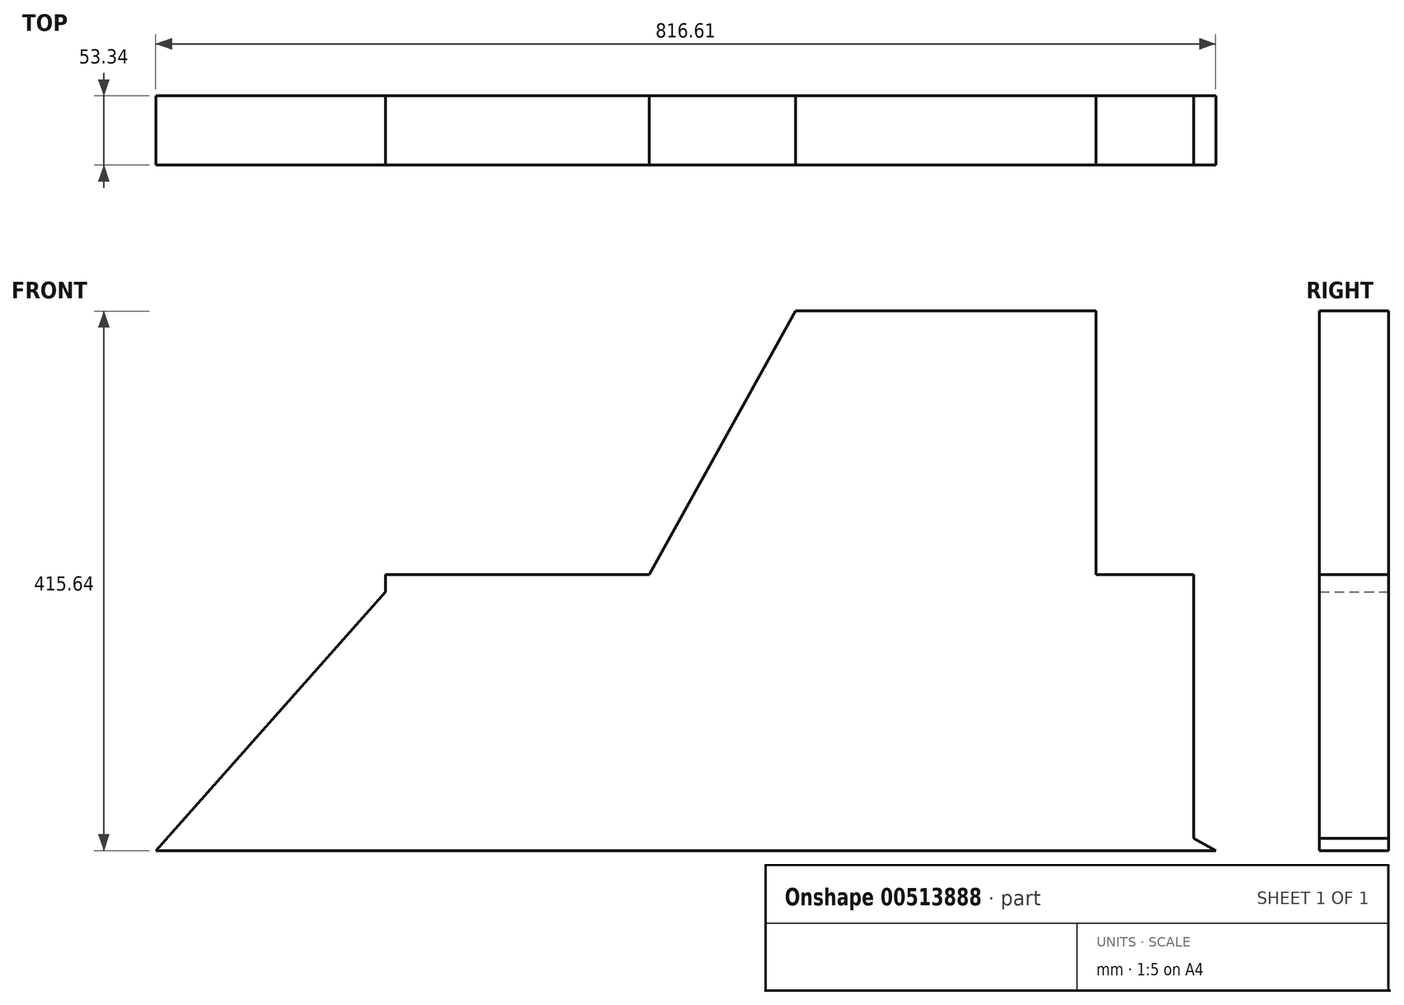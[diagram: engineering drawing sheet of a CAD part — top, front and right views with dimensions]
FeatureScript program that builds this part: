
annotation { "Feature Type Name" : "Feature", "Feature Type Description" : "" }
export const myFeature = defineFeature(function(context is Context, id is Id, definition is map)
    precondition{}
    {
        {
            var Q0;
            Q0=qCreatedBy(makeId("Front.planeOp"),FACE);
            var sketch = newSketch(context, id + "F0", { "sketchPlane" : qUnion([Q0])});
            skLineSegment(sketch, "E0", {"start": v(-76.37, 0) * mm, "end": v(584.03, 0) * mm});
            skLineSegment(sketch, "E1", {"start": v(567.07, 9.24) * mm, "end": v(567.07, 212.44) * mm});
            skLineSegment(sketch, "E2", {"start": v(491.68, 212.44) * mm, "end": v(491.68, 415.64) * mm});
            skLineSegment(sketch, "E3", {"start": v(260.28, 415.64) * mm, "end": v(491.68, 415.64) * mm});
            skLineSegment(sketch, "E4", {"start": v(260.28, 415.64) * mm, "end": v(147.78, 212.44) * mm});
            skLineSegment(sketch, "E5", {"start": v(491.68, 212.44) * mm, "end": v(567.07, 212.44) * mm});
            skLineSegment(sketch, "E6", {"start": v(147.78, 212.44) * mm, "end": v(-55.42, 212.44) * mm});
            skLineSegment(sketch, "E7", {"start": v(-55.42, 199.29) * mm, "end": v(-232.58, 0) * mm});
            skLineSegment(sketch, "E8", {"start": v(-232.58, 0) * mm, "end": v(-55.42, 0) * mm});
            skLineSegment(sketch, "E9", {"start": v(-55.42, 199.29) * mm, "end": v(-55.42, 212.44) * mm});
            skLineSegment(sketch, "E10", {"start": v(567.07, 9.24) * mm, "end": v(584.03, 0) * mm});
            skSolve(sketch);
        }
        {
            var Q0;
            Q0 = qSketchRegion(id + "F0", true);
            extrude(context, id + "F1", {"entities" : qUnion([Q0]), "depth" : 53.34 * mm, "offsetDistance" : 25.4 * mm});
        }
    });
